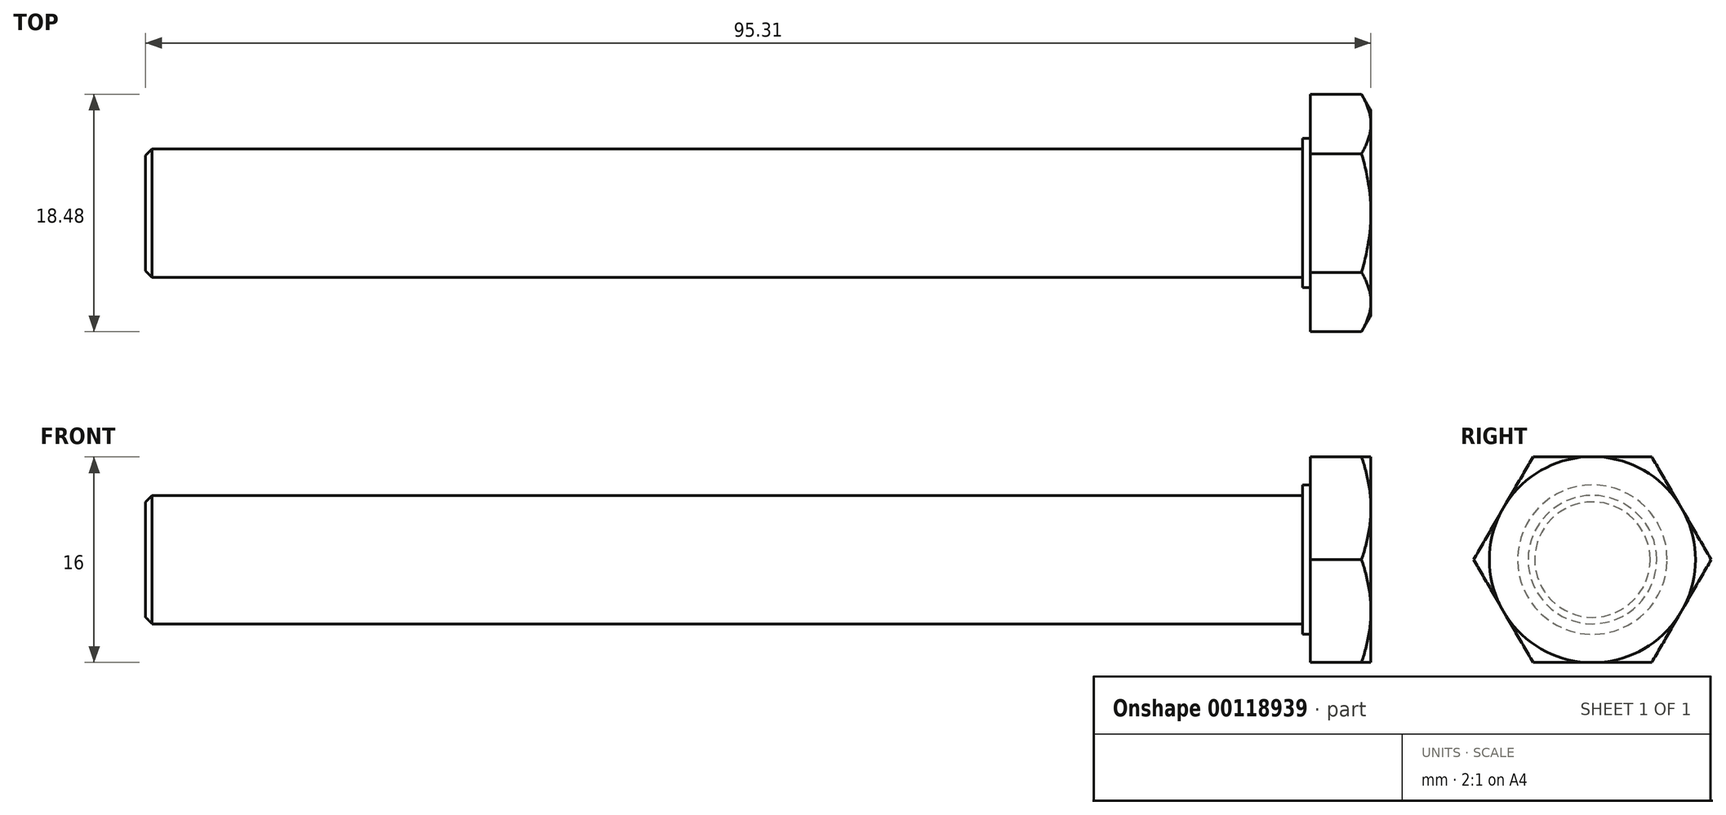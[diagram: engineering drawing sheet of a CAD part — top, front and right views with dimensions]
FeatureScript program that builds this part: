
annotation { "Feature Type Name" : "Feature", "Feature Type Description" : "" }
export const myFeature = defineFeature(function(context is Context, id is Id, definition is map)
    precondition{}
    {
        {
            var Q0;
            Q0=qCreatedBy(makeId("Right.planeOp"),FACE);
            cPlane(context, id + "F0", {"entities" : qUnion([Q0]), "cplaneType" : CPlaneType.OFFSET, "offset" : 152.4 * mm, "width" : 152.4 * mm, "height" : 152.4 * mm});
        }
        {
            var Q0;
            Q0=qCreatedBy(id+"F0.planeOp",FACE);
            var sketch = newSketch(context, id + "F1", { "sketchPlane" : qUnion([Q0])});
            skLineSegment(sketch, "E0", {"start": v(0, 0) * mm, "end": v(0, 2.49) * mm});
            skLineSegment(sketch, "E1", {"start": v(0, 2.49) * mm, "end": v(0.71, 2.49) * mm});
            skLineSegment(sketch, "E2", {"start": v(0.71, 2.49) * mm, "end": v(0.71, 5) * mm});
            skLineSegment(sketch, "E3", {"start": v(0.71, 5) * mm, "end": v(6.2, 5) * mm});
            skLineSegment(sketch, "E4", {"start": v(6.2, 5) * mm, "end": v(6.2, 5.26) * mm});
            skLineSegment(sketch, "E5", {"start": v(6.2, 5.26) * mm, "end": v(9.2, 5.26) * mm});
            skArc(sketch, "E6", {"start": v(9.2, 5.26) * mm, "mid": v(10.15, 3.88) * mm, "end": v(11.45, 2.83) * mm});
            skArc(sketch, "E7", {"start": v(16.3, 0) * mm, "mid": v(14.7, 2.8) * mm, "end": v(11.45, 2.83) * mm});
            skLineSegment(sketch, "E8", {"start": v(0, 0) * mm, "end": v(16.3, 0) * mm});
            skPoint(sketch, "E9.orphan", {"position": v(11.79, 2.64) * mm});
            skSolve(sketch);
        }
        {
            var Q0;
            Q0=makeQuery(id+"F1.imprint","IMPRINT",FACE,{"disambiguationData":[TD([[makeQuery(id+"F1.imprint","IMPRINT",EDGE,{"derivedFrom":sQuery(id+"F1.wireOp",EDGE,"E0")}),-1.0]])]});
            var Q1;
            Q1=sQuery(id+"F1.wireOp",EDGE,"E8");
            revolve(context, id + "F2", {"entities" : qUnion([Q0]), "axis" : qUnion([Q1]), "revolveType" : RevolveType.FULL});
        }
        {
            var Q0;
            Q0=makeQuery(id+"F2.opRevolve","SWEPT_FACE",FACE,{"disambiguationData":[OSD([sQuery(id+"F1.wireOp",EDGE,"E0")])]});
            cPlane(context, id + "F3", {"entities" : qUnion([Q0]), "cplaneType" : CPlaneType.OFFSET, "offset" : 6.2 * mm, "oppositeDirection" : true, "width" : 152.4 * mm, "height" : 152.4 * mm});
        }
        {
            var Q0;
            Q0=qCreatedBy(id+"F3.planeOp",FACE);
            var sketch = newSketch(context, id + "F4", { "sketchPlane" : qUnion([Q0])});
            skPoint(sketch, "E10", {"position": v(152.4, 0) * mm});
            skLineSegment(sketch, "E11", {"start": v(152.4, 0) * mm, "end": v(159.09, 0) * mm, "construction": true});
            skLineSegment(sketch, "E12.0", {"start": v(152.4, -3.18) * mm, "end": v(159.09, -3.18) * mm, "construction": true});
            skLineSegment(sketch, "E13.0", {"start": v(152.4, 3.18) * mm, "end": v(157.9, 3.18) * mm, "construction": true});
            skCircle(sketch, "E14", {"center": v(152.4, 0) * mm, "radius": 5.5 * mm, "construction": true});
            skLineSegment(sketch, "E15", {"start": v(157.9, 3.18) * mm, "end": v(157.9, -3.18) * mm});
            skLineSegment(sketch, "E16", {"start": v(152.4, 7.44) * mm, "end": v(152.4, -7.15) * mm, "construction": true});
            skLineSegment(sketch, "E17.0.MirrorCS", {"start": v(146.9, 3.17) * mm, "end": v(146.9, -3.18) * mm});
            skLineSegment(sketch, "E18", {"start": v(157.9, 3.18) * mm, "end": v(152.4, 6.35) * mm});
            skLineSegment(sketch, "E19.0.MirrorCS", {"start": v(157.9, -3.18) * mm, "end": v(152.4, -6.35) * mm});
            skLineSegment(sketch, "E20.0.MirrorCS", {"start": v(146.9, -3.18) * mm, "end": v(152.4, -6.35) * mm});
            skLineSegment(sketch, "E21", {"start": v(152.4, 6.35) * mm, "end": v(146.9, 3.17) * mm});
            skSolve(sketch);
        }
        {
            var Q0;
            {var subQ4=sQuery(id+"F4.wireOp",EDGE,"E15");Q0=makeQuery(id+"F4.imprint","IMPRINT",FACE,{"disambiguationData":[TD([[makeQuery(id+"F4.imprint","IMPRINT",EDGE,{"derivedFrom":subQ4}),-1.0]])]});}
            extrude(context, id + "F5", {"entities" : qUnion([Q0]), "operationType" : NewBodyOperationType.ADD, "oppositeDirection" : true, "depth" : 3 * mm});
        }
        {
            var Q0;
            Q0=makeQuery(id+"F5.opExtrude","SWEPT_FACE",FACE,{"disambiguationData":[OSD([sQuery(id+"F4.wireOp",EDGE,"E21")])]});
            cPlane(context, id + "F6", {"entities" : qUnion([Q0]), "cplaneType" : CPlaneType.OFFSET, "offset" : 5.5 * mm, "oppositeDirection" : true, "width" : 152.4 * mm, "height" : 152.4 * mm});
        }
        {
            var Q0;
            Q0=qCreatedBy(id+"F6.planeOp",FACE);
            var sketch = newSketch(context, id + "F7", { "sketchPlane" : qUnion([Q0])});
            skLineSegment(sketch, "E22.0", {"start": v(138.33, 6.2) * mm, "end": v(137.48, 6.2) * mm});
            skLineSegment(sketch, "E23", {"start": v(139.63, 7.7) * mm, "end": v(134.5, 7.7) * mm, "construction": true});
            skPoint(sketch, "E24.orphan", {"position": v(135.16, 9.2) * mm});
            skLineSegment(sketch, "E25.0.MirrorCS", {"start": v(137.77, 6.2) * mm, "end": v(138.33, 6.2) * mm});
            skLineSegment(sketch, "E26", {"start": v(138.33, 6.2) * mm, "end": v(137.77, 6.2) * mm});
            skLineSegment(sketch, "E27.0", {"start": v(137.48, 6.2) * mm, "end": v(126.48, 6.2) * mm});
            skLineSegment(sketch, "E28", {"start": v(137.48, 6.2) * mm, "end": v(138.33, 6.4) * mm});
            skPoint(sketch, "E29.orphan", {"position": v(135.16, 6.2) * mm});
            skLineSegment(sketch, "E30", {"start": v(138.33, 6.4) * mm, "end": v(138.33, 6.2) * mm});
            skLineSegment(sketch, "E31", {"start": v(137.48, 6.2) * mm, "end": v(138.33, 6.2) * mm});
            skLineSegment(sketch, "E32.0.MirrorCS", {"start": v(137.48, 9.2) * mm, "end": v(138.33, 9) * mm});
            skLineSegment(sketch, "E33.0.MirrorCS", {"start": v(138.33, 9) * mm, "end": v(138.33, 9.2) * mm});
            skLineSegment(sketch, "E34.0.MirrorCS", {"start": v(138.33, 9.2) * mm, "end": v(137.48, 9.2) * mm});
            skSolve(sketch);
        }
        {
            var Q0;
            {var subQ4=sQuery(id+"F7.wireOp",EDGE,"E28");Q0=makeQuery(id+"F7.imprint","IMPRINT",FACE,{"disambiguationData":[TD([[makeQuery(id+"F7.imprint","IMPRINT",EDGE,{"derivedFrom":subQ4}),-1.0]])]});}
            var Q1;
            Q1=makeQuery(id+"F7.imprint","IMPRINT",FACE,{"disambiguationData":[TD([[makeQuery(id+"F7.imprint","IMPRINT",EDGE,{"derivedFrom":sQuery(id+"F7.wireOp",EDGE,"E32.0.MirrorCS")}),1.0]])]});
            var Q2;
            Q2=sQuery(id+"F4.wireOp",EDGE,"E14");
            revolve(context, id + "F8", {"operationType" : NewBodyOperationType.REMOVE, "entities" : qUnion([Q0, Q1]), "axis" : qUnion([Q2]), "revolveType" : RevolveType.FULL, "oppositeDirection" : true});
        }
        {
            var Q0;
            Q0=qCreatedBy(id+"F3.planeOp",FACE);
            var sketch = newSketch(context, id + "F9", { "sketchPlane" : qUnion([Q0])});
            skCircle(sketch, "E35", {"center": v(152.4, 0) * mm, "radius": 1.02 * mm});
            skSolve(sketch);
        }
        {
            var Q0;
            Q0=makeQuery(id+"F9.imprint","IMPRINT",FACE,{"disambiguationData":[TD([[makeQuery(id+"F9.imprint","IMPRINT",EDGE,{"derivedFrom":sQuery(id+"F9.wireOp",EDGE,"E35")}),1.0]])]});
            var Q1;
            Q1=makeQuery(id+"F2.opRevolve","SWEPT_FACE",FACE,{"disambiguationData":[OSD([sQuery(id+"F1.wireOp",EDGE,"E7")])]});
            extrude(context, id + "F10", {"entities" : qUnion([Q0]), "operationType" : NewBodyOperationType.REMOVE, "endBound" : BoundingType.SYMMETRIC, "oppositeDirection" : true, "endBoundEntity" : qUnion([Q1]), "depth" : 25.4 * mm});
        }
        {
            var Q0;
            Q0=qCreatedBy(id+"F0.planeOp",FACE);
            cPlane(context, id + "F11", {"entities" : qUnion([Q0]), "cplaneType" : CPlaneType.OFFSET, "offset" : 76.2 * mm, "width" : 152.4 * mm, "height" : 152.4 * mm});
        }
        {
            var Q0;
            Q0=qCreatedBy(id+"F11.planeOp",FACE);
            var sketch = newSketch(context, id + "F12", { "sketchPlane" : qUnion([Q0])});
            skCircle(sketch, "E36", {"center": v(0, 0) * mm, "radius": 6.54 * mm});
            skCircle(sketch, "E37", {"center": v(0, 0) * mm, "radius": 4.1 * mm});
            skSolve(sketch);
        }
        {
            var Q0;
            Q0=makeQuery(id+"F12.imprint","IMPRINT",FACE,{"disambiguationData":[TD([[makeQuery(id+"F12.imprint","IMPRINT",EDGE,{"derivedFrom":sQuery(id+"F12.wireOp",EDGE,"E36")}),1.0]])]});
            extrude(context, id + "F13", {"entities" : qUnion([Q0]), "endBound" : BoundingType.SYMMETRIC, "depth" : 1.6 * mm});
        }
        {
            var Q0;
            Q0=qCreatedBy(makeId("Top.planeOp"),FACE);
            cPlane(context, id + "F14", {"entities" : qUnion([Q0]), "cplaneType" : CPlaneType.OFFSET, "offset" : 5.08 * mm, "width" : 152.4 * mm, "height" : 152.4 * mm});
        }
        {
            var Q0;
            Q0=qCreatedBy(id+"F14.planeOp",FACE);
            var sketch = newSketch(context, id + "F15", { "sketchPlane" : qUnion([Q0])});
            skLineSegment(sketch, "E38", {"start": v(0, 0) * mm, "end": v(259.22, 0) * mm, "construction": true});
            skLineSegment(sketch, "E39", {"start": v(229.4, -0.06) * mm, "end": v(227.8, -0.49) * mm});
            skLineSegment(sketch, "E40", {"start": v(227.8, 0.14) * mm, "end": v(229.4, 0.57) * mm});
            skLineSegment(sketch, "E41.0", {"start": v(227.8, 0.14) * mm, "end": v(227.8, -0.49) * mm});
            skPoint(sketch, "E42.orphan", {"position": v(227.8, -6.54) * mm});
            skLineSegment(sketch, "E43.1", {"start": v(229.4, 0.57) * mm, "end": v(229.4, -0.06) * mm});
            skPoint(sketch, "E44.orphan", {"position": v(229.4, 6.54) * mm});
            skPoint(sketch, "E45.orphan", {"position": v(229.4, -6.54) * mm});
            skPoint(sketch, "E46.orphan", {"position": v(227.8, 6.54) * mm});
            skSolve(sketch);
        }
        {
            var Q0;
            Q0=makeQuery(id+"F15.imprint","IMPRINT",FACE,{"disambiguationData":[TD([[makeQuery(id+"F15.imprint","IMPRINT",EDGE,{"derivedFrom":sQuery(id+"F15.wireOp",EDGE,"E39")}),-1.0]])]});
            extrude(context, id + "F16", {"entities" : qUnion([Q0]), "operationType" : NewBodyOperationType.REMOVE, "endBound" : BoundingType.SYMMETRIC, "oppositeDirection" : true, "depth" : 12.7 * mm});
        }
        {
            var Q0;
            Q0=qCreatedBy(id+"F11.planeOp",FACE);
            cPlane(context, id + "F17", {"entities" : qUnion([Q0]), "cplaneType" : CPlaneType.OFFSET, "offset" : 50.8 * mm, "width" : 152.4 * mm, "height" : 152.4 * mm});
        }
        {
            var Q0;
            Q0=qCreatedBy(id+"F17.planeOp",FACE);
            var sketch = newSketch(context, id + "F18", { "sketchPlane" : qUnion([Q0])});
            skCircle(sketch, "E47", {"center": v(0, 0) * mm, "radius": 5 * mm});
            skSolve(sketch);
        }
        {
            var Q0;
            Q0=makeQuery(id+"F18.imprint","IMPRINT",FACE,{"disambiguationData":[TD([[makeQuery(id+"F18.imprint","IMPRINT",EDGE,{"derivedFrom":sQuery(id+"F18.wireOp",EDGE,"E47")}),1.0]])]});
            extrude(context, id + "F19", {"entities" : qUnion([Q0]), "depth" : 90 * mm});
        }
        {
            var Q0;
            Q0=makeQuery(id+"F19.opExtrude","CAP_FACE",FACE,{"disambiguationData":[OSD([sQuery(id+"F18.wireOp",EDGE,"E47")])],"isStart":false});
            var sketch = newSketch(context, id + "F20", { "sketchPlane" : qUnion([Q0])});
            skCircle(sketch, "E48", {"center": v(0, 0) * mm, "radius": 5.82 * mm});
            skSolve(sketch);
        }
        {
            var Q0;
            {var subQ0=makeQuery(id+"F20.imprint","IMPRINT",EDGE,{"derivedFrom":makeQuery(id+"F19.opExtrude","CAP_EDGE",EDGE,{"disambiguationData":[OSD([sQuery(id+"F18.wireOp",EDGE,"E47")])],"isStart":false})});Q0=qUnion([makeQuery(id+"F20.imprint","IMPRINT",FACE,{"disambiguationData":[TD([[makeQuery(id+"F20.imprint","IMPRINT",EDGE,{"derivedFrom":sQuery(id+"F20.wireOp",EDGE,"E48")}),1.0]])]}),makeQuery(id+"F20.imprint","IMPRINT",FACE,{"disambiguationData":[TD([[subQ0,1.0]])]})]);}
            extrude(context, id + "F21", {"entities" : qUnion([Q0]), "operationType" : NewBodyOperationType.ADD, "depth" : 0.6 * mm});
        }
        {
            var Q0;
            Q0=makeQuery(id+"F21.opExtrude","CAP_FACE",FACE,{"disambiguationData":[OSD([sQuery(id+"F20.wireOp",EDGE,"E48")])],"isStart":false});
            var sketch = newSketch(context, id + "F22", { "sketchPlane" : qUnion([Q0])});
            skCircle(sketch, "E49", {"center": v(0, 0) * mm, "radius": 8 * mm, "construction": true});
            skLineSegment(sketch, "E50", {"start": v(0, 0) * mm, "end": v(0, 10.8) * mm, "construction": true});
            skLineSegment(sketch, "E51", {"start": v(0, 0) * mm, "end": v(-10.31, 0) * mm, "construction": true});
            skLineSegment(sketch, "E52", {"start": v(-4.62, 8) * mm, "end": v(4.62, 8) * mm});
            skLineSegment(sketch, "E53", {"start": v(-4.62, 8) * mm, "end": v(-9.24, 0) * mm});
            skLineSegment(sketch, "E54.0.MirrorCS", {"start": v(4.62, 8) * mm, "end": v(9.24, 0) * mm});
            skLineSegment(sketch, "E55.0.MirrorCS", {"start": v(-4.62, -8) * mm, "end": v(-9.24, 0) * mm});
            skLineSegment(sketch, "E56.0.MirrorCS", {"start": v(4.62, -8) * mm, "end": v(9.24, 0) * mm});
            skLineSegment(sketch, "E57.0.MirrorCS", {"start": v(-4.62, -8) * mm, "end": v(4.62, -8) * mm});
            skSolve(sketch);
        }
        {
            var Q0;
            {var subQ0=makeQuery(id+"F22.imprint","IMPRINT",EDGE,{"derivedFrom":makeQuery(id+"F21.opExtrude","CAP_EDGE",EDGE,{"disambiguationData":[OSD([sQuery(id+"F20.wireOp",EDGE,"E48")])],"isStart":false})});Q0=qUnion([makeQuery(id+"F22.imprint","IMPRINT",FACE,{"disambiguationData":[TD([[makeQuery(id+"F22.imprint","IMPRINT",EDGE,{"derivedFrom":sQuery(id+"F22.wireOp",EDGE,"E52")}),-1.0]])]}),makeQuery(id+"F22.imprint","IMPRINT",FACE,{"disambiguationData":[TD([[subQ0,1.0]])]})]);}
            var Q1;
            Q1=sQuery(id+"F22.wireOp",EDGE,"E52");
            extrude(context, id + "F23", {"entities" : qUnion([Q0]), "operationType" : NewBodyOperationType.ADD, "surfaceEntities" : qUnion([Q1]), "depth" : 4.7 * mm});
        }
        {
            var Q0;
            Q0=makeQuery(id+"F23.opExtrude","SWEPT_FACE",FACE,{"disambiguationData":[OSD([sQuery(id+"F22.wireOp",EDGE,"E55.0.MirrorCS")])]});
            cPlane(context, id + "F24", {"entities" : qUnion([Q0]), "cplaneType" : CPlaneType.OFFSET, "offset" : 6.5 * mm, "oppositeDirection" : true, "width" : 152.4 * mm, "height" : 152.4 * mm});
        }
        {
            var Q0;
            Q0=qCreatedBy(id+"F24.planeOp",FACE);
            var sketch = newSketch(context, id + "F25", { "sketchPlane" : qUnion([Q0])});
            skPoint(sketch, "E58.orphan", {"position": v(370, 9.24) * mm});
            skPoint(sketch, "E59", {"position": v(374.7, 7.87) * mm});
            skLineSegment(sketch, "E60", {"start": v(374.7, 7.87) * mm, "end": v(374.7, 9.24) * mm});
            skLineSegment(sketch, "E61", {"start": v(374.7, 7.87) * mm, "end": v(373.92, 9.24) * mm});
            skLineSegment(sketch, "E62.0", {"start": v(374.7, 9.24) * mm, "end": v(373.92, 9.24) * mm});
            skSolve(sketch);
        }
        {
            var Q0;
            Q0=makeQuery(id+"F25.imprint","IMPRINT",FACE,{"disambiguationData":[TD([[makeQuery(id+"F25.imprint","IMPRINT",EDGE,{"derivedFrom":sQuery(id+"F25.wireOp",EDGE,"E60")}),1.0]])]});
            var Q1;
            Q1=sQuery(id+"F22.wireOp",EDGE,"E49");
            revolve(context, id + "F26", {"operationType" : NewBodyOperationType.REMOVE, "entities" : qUnion([Q0]), "axis" : qUnion([Q1]), "revolveType" : RevolveType.FULL, "oppositeDirection" : true});
        }
        {
            var Q0;
            Q0=makeQuery(id+"F19.opExtrude","CAP_EDGE",EDGE,{"disambiguationData":[OSD([sQuery(id+"F18.wireOp",EDGE,"E47")])],"isStart":true});
            chamfer(context, id + "F27", {"entities" : qUnion([Q0]), "width" : 0.5 * mm, "tangentPropagation" : true});
        }
        {
            var Q0;
            Q0=makeQuery(id+"F13.opExtrude","SWEPT_BODY",BODY,{"disambiguationData":[OSD([sQuery(id+"F12.wireOp",EDGE,"E36"),sQuery(id+"F12.wireOp",EDGE,"E37")])]});
            var Q1;
            Q1=makeQuery(id+"F2.opRevolve","SWEPT_BODY",BODY,{"disambiguationData":[OSD([sQuery(id+"F1.wireOp",EDGE,"E0"),sQuery(id+"F1.wireOp",EDGE,"E1"),sQuery(id+"F1.wireOp",EDGE,"E2"),sQuery(id+"F1.wireOp",EDGE,"E3"),sQuery(id+"F1.wireOp",EDGE,"E4"),sQuery(id+"F1.wireOp",EDGE,"E5"),sQuery(id+"F1.wireOp",EDGE,"E6"),sQuery(id+"F1.wireOp",EDGE,"E7"),sQuery(id+"F1.wireOp",EDGE,"E8")])]});
            deleteBodies(context, id + "F28", {"entities" : qUnion([Q0, Q1])});
        }
    });
